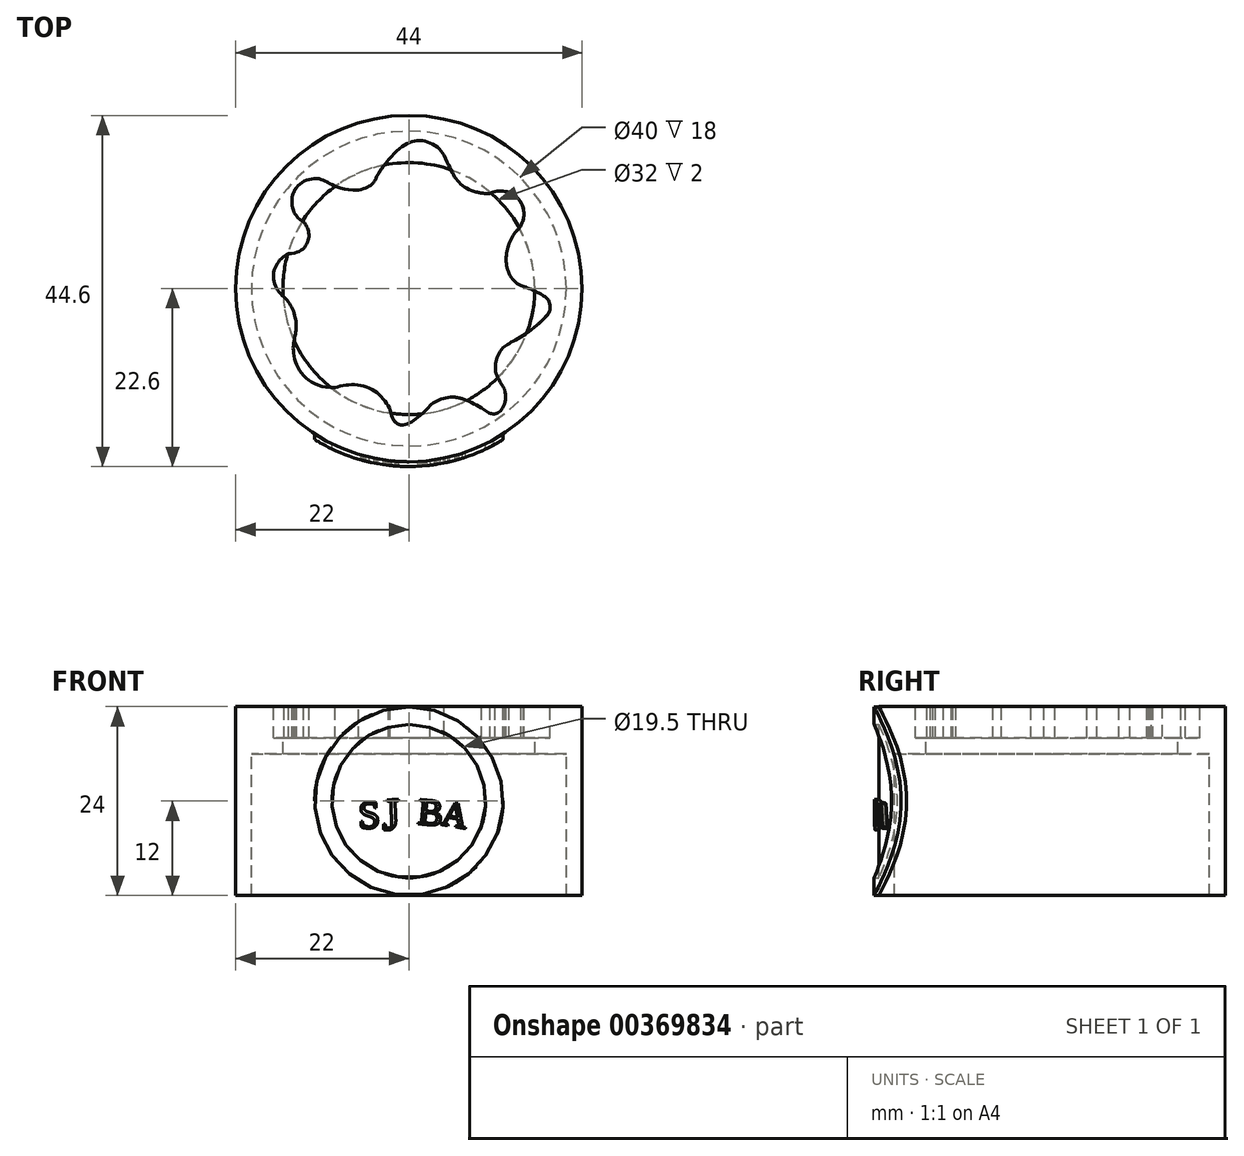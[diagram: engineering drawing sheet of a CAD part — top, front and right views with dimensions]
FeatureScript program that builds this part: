
annotation { "Feature Type Name" : "Feature", "Feature Type Description" : "" }
export const myFeature = defineFeature(function(context is Context, id is Id, definition is map)
    precondition{}
    {
        {
            var Q0;
            Q0=qCreatedBy(makeId("Top.planeOp"),FACE);
            var Q1;
            Q1=qBodyType(qCreatedBy(id+"F1",EDGE),BodyType.WIRE);
            cPlane(context, id + "F0", {"entities" : qUnion([Q0, Q1]), "cplaneType" : CPlaneType.OFFSET, "offset" : 12 * mm, "width" : 150 * mm, "height" : 150 * mm});
        }
        {
            var Q0;
            Q0=qCreatedBy(id+"F0.planeOp",FACE);
            var sketch = newSketch(context, id + "F1", { "sketchPlane" : qUnion([Q0])});
            skCircle(sketch, "E0", {"center": v(0, 0) * mm, "radius": 22 * mm});
            skFitSpline(sketch, "E1", {"points": [v(-14.3, 12.84) * mm, v(-11.44, 13.95) * mm, v(-6.4, 12.53) * mm], "startDerivative": vector(4.46, 5.6) * mm, "endDerivative": vector(16.32, 0.58) * mm});
            skFitSpline(sketch, "E2", {"points": [v(-14.3, 12.84) * mm, v(-14.8, 10.36) * mm, v(-13.38, 8.48) * mm], "startDerivative": vector(-2.91, -3.74) * mm, "endDerivative": vector(4.44, -2.3) * mm});
            skFitSpline(sketch, "E3", {"points": [v(-13.38, 8.48) * mm, v(-12.7, 6.62) * mm, v(-15.26, 4.45) * mm], "startDerivative": vector(2.5, -2.67) * mm, "endDerivative": vector(-9.07, 0.1) * mm});
            skFitSpline(sketch, "E4", {"points": [v(-15.26, 4.45) * mm, v(-17.17, 1.96) * mm, v(-15.87, -1.05) * mm], "startDerivative": vector(-5.88, -2.54) * mm, "endDerivative": vector(5.37, -3.99) * mm});
            skFitSpline(sketch, "E5", {"points": [v(-15.87, -1.05) * mm, v(-14.36, -3.98) * mm, v(-14.54, -6.45) * mm], "startDerivative": vector(4.6, -4.23) * mm, "endDerivative": vector(-1.12, -5.28) * mm});
            skFitSpline(sketch, "E6", {"points": [v(-14.54, -6.45) * mm, v(-14.3, -9.6) * mm, v(-9.38, -12.57) * mm], "startDerivative": vector(-1.49, -4.88) * mm, "endDerivative": vector(14.07, 0.6) * mm});
            skFitSpline(sketch, "E7", {"points": [v(-9.38, -12.57) * mm, v(-5.16, -12.57) * mm, v(-2.36, -15.43) * mm], "startDerivative": vector(7.18, 2.12) * mm, "endDerivative": vector(2.53, -6.19) * mm});
            skFitSpline(sketch, "E8", {"points": [v(-2.36, -15.43) * mm, v(-0.75, -17.32) * mm, v(2.7, -14.82) * mm], "startDerivative": vector(1.67, -9.42) * mm, "endDerivative": vector(5.03, 5.85) * mm});
            skFitSpline(sketch, "E9", {"points": [v(2.7, -14.82) * mm, v(5.45, -13.78) * mm, v(9.22, -15.14) * mm], "startDerivative": vector(4.06, 3.24) * mm, "endDerivative": vector(7.18, -3.93) * mm});
            skFitSpline(sketch, "E10", {"points": [v(9.22, -15.14) * mm, v(11.11, -15.85) * mm, v(12.13, -12.78) * mm], "startDerivative": vector(4.38, -3.77) * mm, "endDerivative": vector(-2.9, 8.35) * mm});
            skFitSpline(sketch, "E11", {"points": [v(12.13, -12.78) * mm, v(11.06, -10.66) * mm, v(11.96, -7.51) * mm], "startDerivative": vector(-1.65, 4.16) * mm, "endDerivative": vector(4.57, 5.25) * mm});
            skFitSpline(sketch, "E12", {"points": [v(11.96, -7.51) * mm, v(14.65, -5.88) * mm, v(17.91, -2.7) * mm], "startDerivative": vector(3.62, 3.57) * mm, "endDerivative": vector(-0.15, 3.1) * mm});
            skFitSpline(sketch, "E13", {"points": [v(17.91, -2.7) * mm, v(16.74, -0.7) * mm, v(14.28, 0.37) * mm], "startDerivative": vector(0.98, 7.59) * mm, "endDerivative": vector(-4.1, 1.2) * mm});
            skFitSpline(sketch, "E14", {"points": [v(14.28, 0.37) * mm, v(12.43, 2.83) * mm, v(12.74, 5.73) * mm], "startDerivative": vector(-6.41, 2.8) * mm, "endDerivative": vector(2.08, 5.38) * mm});
            skFitSpline(sketch, "E15", {"points": [v(12.74, 5.73) * mm, v(14.05, 7.73) * mm, v(14.57, 9.89) * mm], "startDerivative": vector(4.72, 10.1) * mm, "endDerivative": vector(-1.17, 4.74) * mm});
            skFitSpline(sketch, "E16", {"points": [v(14.57, 9.89) * mm, v(13.17, 12.02) * mm, v(10.32, 12.08) * mm], "startDerivative": vector(0.08, 3.85) * mm, "endDerivative": vector(-4.12, -2.28) * mm});
            skFitSpline(sketch, "E17", {"points": [v(10.32, 12.08) * mm, v(6.46, 13.4) * mm, v(4.44, 16.97) * mm], "startDerivative": vector(-9.93, -0.41) * mm, "endDerivative": vector(-5.62, 10.83) * mm});
            skFitSpline(sketch, "E18", {"points": [v(4.44, 16.97) * mm, v(1.52, 18.8) * mm, v(-2.58, 16.4) * mm], "startDerivative": vector(-2.9, 6.35) * mm, "endDerivative": vector(-8.38, -9.56) * mm});
            skFitSpline(sketch, "E19", {"points": [v(-2.58, 16.4) * mm, v(-4.36, 13.61) * mm, v(-6.4, 12.53) * mm], "startDerivative": vector(-9.43, -11.95) * mm, "endDerivative": vector(-8.2, -1.4) * mm});
            skCircle(sketch, "E20", {"center": v(0, 0) * mm, "radius": 20 * mm});
            skSolve(sketch);
        }
        {
            var Q0;
            Q0=qCreatedBy(makeId("Top.planeOp"),FACE);
            cPlane(context, id + "F2", {"entities" : qUnion([Q0]), "cplaneType" : CPlaneType.OFFSET, "offset" : 8 * mm, "width" : 150 * mm, "height" : 150 * mm});
        }
        {
            var Q0;
            Q0=qCreatedBy(id+"F2.planeOp",FACE);
            var sketch = newSketch(context, id + "F3", { "sketchPlane" : qUnion([Q0])});
            skCircle(sketch, "E21", {"center": v(0, 0) * mm, "radius": 20 * mm});
            skCircle(sketch, "E22", {"center": v(0, 0) * mm, "radius": 16 * mm});
            skSolve(sketch);
        }
        {
            var Q0;
            Q0=makeQuery(id+"F1.imprint","IMPRINT",FACE,{"disambiguationData":[TD([[makeQuery(id+"F1.imprint","IMPRINT",EDGE,{"derivedFrom":sQuery(id+"F1.wireOp",EDGE,"E1")}),1.0]])]});
            extrude(context, id + "F4", {"entities" : qUnion([Q0]), "oppositeDirection" : true, "depth" : 4 * mm});
        }
        {
            var Q0;
            Q0=makeQuery(id+"F1.imprint","IMPRINT",FACE,{"disambiguationData":[TD([[makeQuery(id+"F1.imprint","IMPRINT",EDGE,{"derivedFrom":sQuery(id+"F1.wireOp",EDGE,"E0")}),1.0]])]});
            extrude(context, id + "F5", {"entities" : qUnion([Q0]), "operationType" : NewBodyOperationType.ADD, "oppositeDirection" : true, "depth" : 24 * mm});
        }
        {
            var Q0;
            Q0=makeQuery(id+"F3.imprint","IMPRINT",FACE,{"disambiguationData":[TD([[makeQuery(id+"F3.imprint","IMPRINT",EDGE,{"derivedFrom":sQuery(id+"F3.wireOp",EDGE,"E21")}),1.0]])]});
            extrude(context, id + "F6", {"entities" : qUnion([Q0]), "operationType" : NewBodyOperationType.ADD, "oppositeDirection" : true, "depth" : 2 * mm});
        }
        {
            var Q0;
            Q0=qCreatedBy(id+"F0.planeOp",FACE);
            var sketch = newSketch(context, id + "F7", { "sketchPlane" : qUnion([Q0])});
            skCircle(sketch, "E23", {"center": v(0, 0) * mm, "radius": 22.6 * mm});
            skSolve(sketch);
        }
        {
            var Q0;
            Q0=qSketchRegion(id+"F7",true);
            var Q1;
            Q1=qConstructionFilter(qBodyType(qCreatedBy(id+"F7",EDGE),BodyType.WIRE),ConstructionObject.NO);
            extrude(context, id + "F8", {"entities" : qUnion([Q0]), "bodyType" : ToolBodyType.SURFACE, "operationType" : NewBodyOperationType.ADD, "surfaceEntities" : qUnion([Q1]), "oppositeDirection" : true, "depth" : 24 * mm});
        }
        {
            var Q0;
            Q0=qCreatedBy(makeId("Front.planeOp"),FACE);
            var sketch = newSketch(context, id + "F9", { "sketchPlane" : qUnion([Q0])});
            skCircle(sketch, "E24", {"center": v(0, 0) * mm, "radius": 11.96 * mm});
            skCircle(sketch, "E25", {"center": v(0, 0) * mm, "radius": 9.75 * mm});
            skFitSpline(sketch, "E26", {"points": [v(-1.47, 8.86) * mm, v(0, 9.04) * mm, v(1.48, 8.86) * mm], "startDerivative": vector(3, 0.68) * mm, "endDerivative": vector(3.93, -0.85) * mm});
            skFitSpline(sketch, "E27", {"points": [v(-0.87, 8.42) * mm, v(-0.57, 8.5) * mm, v(-0.22, 8.52) * mm], "startDerivative": vector(1.2, 0.45) * mm, "endDerivative": vector(1.18, -0.12) * mm});
            skFitSpline(sketch, "E28", {"points": [v(0.18, 8.53) * mm, v(0.53, 8.5) * mm, v(0.84, 8.4) * mm], "startDerivative": vector(0.7, -0.01) * mm, "endDerivative": vector(0.62, -0.25) * mm});
            skFitSpline(sketch, "E29", {"points": [v(-0.87, 8.42) * mm, v(-0.32, 6.7) * mm, v(-0.13, 4.87) * mm], "startDerivative": vector(1.28, -3.42) * mm, "endDerivative": vector(0.2, -3.67) * mm});
            skFitSpline(sketch, "E30", {"points": [v(-0.22, 8.52) * mm, v(-0.13, 6.64) * mm, v(-0.13, 4.87) * mm], "startDerivative": vector(0.5, -4.14) * mm, "endDerivative": vector(-0.26, -3.4) * mm});
            skFitSpline(sketch, "E31", {"points": [v(0.18, 8.53) * mm, v(0.1, 6.6) * mm, v(0.12, 4.87) * mm], "startDerivative": vector(-0.54, -4.13) * mm, "endDerivative": vector(0.3, -3.43) * mm});
            skFitSpline(sketch, "E32", {"points": [v(0.84, 8.4) * mm, v(0.3, 6.68) * mm, v(0.12, 4.87) * mm], "startDerivative": vector(-1.26, -3.07) * mm, "endDerivative": vector(-0.2, -3.65) * mm});
            skFitSpline(sketch, "E33", {"points": [v(-1.47, 8.86) * mm, v(-1.06, 6.41) * mm, v(-0.82, 4.05) * mm], "startDerivative": vector(1.14, -5.23) * mm, "endDerivative": vector(0.16, -4.54) * mm});
            skFitSpline(sketch, "E34", {"points": [v(1.48, 8.86) * mm, v(1, 6.27) * mm, v(0.78, 4.04) * mm], "startDerivative": vector(-1.43, -5.77) * mm, "endDerivative": vector(-0.17, -4.58) * mm});
            skFitSpline(sketch, "E35", {"points": [v(0.78, 4.04) * mm, v(3.45, 4.3) * mm, v(6.35, 4.86) * mm], "startDerivative": vector(5.44, 0.37) * mm, "endDerivative": vector(5.7, 1.27) * mm});
            skFitSpline(sketch, "E36", {"points": [v(6.35, 4.86) * mm, v(6.99, 3.1) * mm, v(6.35, 1.1) * mm], "startDerivative": vector(1.93, -3.57) * mm, "endDerivative": vector(-1.9, -3.93) * mm});
            skFitSpline(sketch, "E37", {"points": [v(6.35, 1.1) * mm, v(3.34, 2.2) * mm, v(0.77, 2.65) * mm], "startDerivative": vector(-5.8, 2.4) * mm, "endDerivative": vector(-5.35, 0.66) * mm});
            skFitSpline(sketch, "E38", {"points": [v(-0.82, 4.05) * mm, v(-3.51, 4.32) * mm, v(-6.23, 4.86) * mm], "startDerivative": vector(-6.24, 0.07) * mm, "endDerivative": vector(-5.41, 1.18) * mm});
            skFitSpline(sketch, "E39", {"points": [v(-6.23, 4.86) * mm, v(-6.92, 3.03) * mm, v(-6.23, 1.07) * mm], "startDerivative": vector(-2.07, -3.68) * mm, "endDerivative": vector(2.05, -3.9) * mm});
            skFitSpline(sketch, "E40", {"points": [v(-6.23, 1.07) * mm, v(-3.54, 2.1) * mm, v(-0.72, 2.64) * mm], "startDerivative": vector(5.31, 2.3) * mm, "endDerivative": vector(5.67, 0.12) * mm});
            skFitSpline(sketch, "E41", {"points": [v(-0.72, 2.64) * mm, v(-0.94, -3.18) * mm, v(-2.1, -8.88) * mm], "startDerivative": vector(0.03, -11.7) * mm, "endDerivative": vector(-2.8, -11.35) * mm});
            skFitSpline(sketch, "E42", {"points": [v(0.77, 2.65) * mm, v(1.08, -3.2) * mm, v(2.02, -8.89) * mm], "startDerivative": vector(-0.63, -11.75) * mm, "endDerivative": vector(2.63, -11.18) * mm});
            skFitSpline(sketch, "E43", {"points": [v(-2.1, -8.88) * mm, v(0, -9.25) * mm, v(2.02, -8.89) * mm], "startDerivative": vector(4.18, -1.1) * mm, "endDerivative": vector(4.06, 1.1) * mm});
            skFitSpline(sketch, "E44", {"points": [v(-0.2, -0.13) * mm, v(-0.54, -4.77) * mm, v(-1.34, -8.45) * mm], "startDerivative": vector(-0.4, -9.09) * mm, "endDerivative": vector(-1.92, -7.53) * mm});
            skFitSpline(sketch, "E45", {"points": [v(-0.2, -0.13) * mm, v(-0.2, -4.68) * mm, v(-0.37, -8.58) * mm], "startDerivative": vector(0.1, -8.93) * mm, "endDerivative": vector(-0.46, -7.96) * mm});
            skFitSpline(sketch, "E46", {"points": [v(-1.34, -8.45) * mm, v(-0.84, -8.57) * mm, v(-0.37, -8.58) * mm], "startDerivative": vector(0.98, -0.28) * mm, "endDerivative": vector(0.96, 0.02) * mm});
            skFitSpline(sketch, "E47", {"points": [v(0.2, -0.16) * mm, v(0.53, -4.76) * mm, v(1.28, -8.44) * mm], "startDerivative": vector(0.36, -9) * mm, "endDerivative": vector(1.81, -7.52) * mm});
            skFitSpline(sketch, "E48", {"points": [v(0.2, -0.16) * mm, v(0.2, -4.74) * mm, v(0.28, -8.55) * mm], "startDerivative": vector(-0.8, -10.06) * mm, "endDerivative": vector(0.8, -6.07) * mm});
            skFitSpline(sketch, "E49", {"points": [v(-6, 4.23) * mm, v(-6.4, 3.02) * mm, v(-6.03, 1.8) * mm], "startDerivative": vector(-2.04, -2) * mm, "endDerivative": vector(1.56, -2.23) * mm});
            skFitSpline(sketch, "E50", {"points": [v(-6, 4.23) * mm, v(-4.59, 3.53) * mm, v(-2.53, 3.24) * mm], "startDerivative": vector(2.9, -2.4) * mm, "endDerivative": vector(4.07, -0.27) * mm});
            skFitSpline(sketch, "E51", {"points": [v(-6.03, 1.8) * mm, v(-4.65, 2.78) * mm, v(-2.53, 3.24) * mm], "startDerivative": vector(1.56, 3.04) * mm, "endDerivative": vector(4.27, 0.54) * mm});
            skFitSpline(sketch, "E52", {"points": [v(2.43, 3.22) * mm, v(4.45, 3.48) * mm, v(5.95, 4.21) * mm], "startDerivative": vector(4.02, 0.22) * mm, "endDerivative": vector(2.43, 2.2) * mm});
            skFitSpline(sketch, "E53", {"points": [v(2.43, 3.22) * mm, v(4.46, 2.8) * mm, v(5.96, 1.78) * mm], "startDerivative": vector(4.13, -0.5) * mm, "endDerivative": vector(2.55, -3.62) * mm});
            skFitSpline(sketch, "E54", {"points": [v(5.95, 4.21) * mm, v(6.32, 2.99) * mm, v(5.96, 1.78) * mm], "startDerivative": vector(1.87, -2.43) * mm, "endDerivative": vector(-1.75, -2.22) * mm});
            skFitSpline(sketch, "E55", {"points": [v(0.28, -8.55) * mm, v(0.81, -8.55) * mm, v(1.28, -8.44) * mm], "startDerivative": vector(1.05, -0.06) * mm, "endDerivative": vector(0.94, 0.27) * mm});
            skSolve(sketch);
        }
        {
            var Q0;
            Q0=qCreatedBy(makeId("Front.planeOp"),FACE);
            var sketch = newSketch(context, id + "F10", { "sketchPlane" : qUnion([Q0])});
            skText(sketch, "E56", { "text": "S", "fontName": "Tinos-Regular.ttf"});
            skText(sketch, "E57", { "text": "J", "fontName": "Tinos-Regular.ttf"});
            skText(sketch, "E58", { "text": "B", "fontName": "Tinos-Regular.ttf"});
            skText(sketch, "E59", { "text": "A", "fontName": "Tinos-Regular.ttf"});
            const initialGuessF10  = {"E56": [-0.00637, -0.00345, 0.99966, 0.02625, 0.00357], "E57": [-0.0033, -0.00366, 0.99908, 0.04292, 0.00416], "E58": [0.00105, -0.00288, 0.9961, -0.0882, 0.0034], "E59": [0.00398, -0.00296, 0.98638, -0.1645, 0.00326]};
            skSetInitialGuess(sketch, initialGuessF10);
            skSolve(sketch);
        }
        {
            var Q0;
            Q0=makeQuery(id+"F9.imprint","IMPRINT",FACE,{"disambiguationData":[TD([[makeQuery(id+"F9.imprint","IMPRINT",EDGE,{"derivedFrom":sQuery(id+"F9.wireOp",EDGE,"E24")}),1.0]])]});
            var Q1;
            Q1=makeQuery(id+"F9.imprint","IMPRINT",FACE,{"disambiguationData":[TD([[makeQuery(id+"F9.imprint","IMPRINT",EDGE,{"derivedFrom":sQuery(id+"F9.wireOp",EDGE,"2ddbdf16-63be-47a9-8e58-61b453a4f4b2")}),-1.0]])]});
            var Q2;
            Q2=qSketchRegion(id+"F10",true);
            var Q3;
            Q3=makeQuery(id+"F8.opExtrude","SWEPT_FACE",FACE,{"disambiguationData":[OSD([sQuery(id+"F7.wireOp",EDGE,"E23")])]});
            var Q4;
            Q4=makeQuery(id+"F5.opExtrude","SWEPT_FACE",FACE,{"disambiguationData":[OSD([sQuery(id+"F1.wireOp",EDGE,"E0")])]});
            extrude(context, id + "F11", {"entities" : qUnion([Q0, Q1, Q2]), "operationType" : NewBodyOperationType.ADD, "endBound" : BoundingType.UP_TO_SURFACE, "endBoundEntityFace" : qUnion([Q3]), "depth" : 25 * mm, "hasSecondDirection" : true, "secondDirectionBound" : SecondDirectionBoundingType.UP_TO_SURFACE, "secondDirectionOppositeDirection" : false, "secondDirectionBoundEntityFace" : qUnion([Q4]), "secondDirectionDepth" : 25 * mm});
        }
    });
